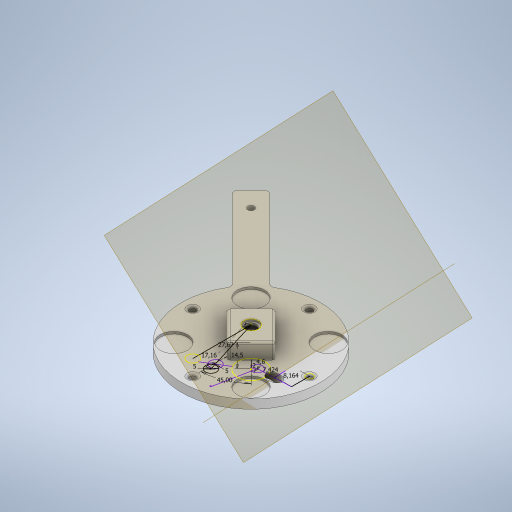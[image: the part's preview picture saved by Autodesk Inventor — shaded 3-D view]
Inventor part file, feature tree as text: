
AUTODESK INVENTOR PART (.ipt)
format: ipt  version: 2024 (Build 280153000, 153)  size: 437,248 bytes
history: native  units: in
note: dims shown in document units (in); Inventor stores cm internally (conversion verified against a paired STEP export)
features: sketch x19, extrude x12, fillet x2, other x1, plane x1
ambient origin geometry x8: Origin, YZ Plane, XZ Plane, XY Plane, X Axis, Y Axis, Z Axis, Center Point
bodies: Solid1 (feature_tree)
feature tree (35):
  extrude  "Plate"  Depth=0.1575in TaperAngle=0.0deg
  extrude  "Lens hole"  Depth=0.0787in TaperAngle=0.0deg
  extrude  "Optical hole"  Depth=0.0787in TaperAngle=0.0deg
  extrude  "Screw holes"  Depth=0.1969in
  sketch  "Sketch6"  dims[d11=1.5748in d13=360.0deg d15=0.1575in d16=0.0in]
  extrude  "Extrusion6"  Depth=0.1575in TaperAngle=0.0deg
  extrude  "Extrusion7"  TaperAngle=45.0deg  [1 undecoded]
  extrude  "Extrusion8"  Depth=0.6102in
  extrude  "Extrusion9"  Depth=0.0787in
  fillet  "Fillet1"  Radius=0.6102in
  extrude  "Magnet holdes"  Depth=0.0787in TaperAngle=0.0deg
  sketch  "Sketch12"  dims[d39=0.1969in d40=0.0394in d41=0.0in d42=0.0394in]
  sketch  "Sketch13"  dims[d43=45.0deg d44=0.2638in]
  extrude  "Extrusion12"  Depth=0.0394in TaperAngle=0.0deg
  extrude  "Extrusion13"  Depth=0.0394in TaperAngle=0.0deg
  fillet  "Fillet2"  Radius=0.0394in
  sketch  "Sketch16"  dims[d50=0.0394in d51=0.0in]
  sketch  "Sketch17"  dims[d52=0.1969in]
  sketch  "Sketch18"  dims[d55=0.2362in]
  sketch  "Sketch19"  dims[d56=0.2362in]
  other  "Work Axis1"
  plane  "Work Plane1"
  extrude  "Extrusion15"  Depth=0.2638in
  sketch  "Sketch1"  dims[d0=2.4803in d1=0.1575in d2=0.0in]
  sketch  "Sketch2"  dims[d3=0.5236in d4=0.0787in d5=0.0in]
  sketch  "Sketch3"  dims[d6=0.3937in d7=0.0787in d8=0.0in]
  sketch  "Sketch4"  dims[d9=0.1969in d10=0.122in]
  sketch  "Sketch7"  dims[d25=0.3051in d26=45.0deg]
  sketch  "Sketch8"  dims[d27=0.0787in d28=0.6102in]
  sketch  "Sketch9"  dims[d29=0.3051in d30=0.0787in d31=0.6102in]
  sketch  "Sketch10"  dims[d32=0.1969in d33=0.0in d34=0.0787in d35=0.0in]
  sketch  "Sketch11"  dims[d36=0.2598in d37=0.0394in d38=0.0in]
  sketch  "Sketch14"  dims[d45=0.4882in]
  sketch  "Sketch15"  dims[d46=1.5748in d48=360.0deg]
  sketch  "Sketch20"  dims[d57=2.3622in d58=0.1575in d59=0.0in d61=0.3937in d62=0.1181in d63=0.1575in d64=0.0in d65=0.0787in d67=1.0894in d68=0.1179in d69=0.1969in d72=0.5709in d73=45.0deg d74=0.0787in d75=0.1811in d76=0.3214in d77=0.2923in d78=45.0deg d79=0.1969in d80=0.6693in d81=0.0in]
note: 1 required parameter value undecoded (feature->parameter linkage not recoverable at this tier; creation-order binding heuristic only, values carry confidence <= 0.55)
